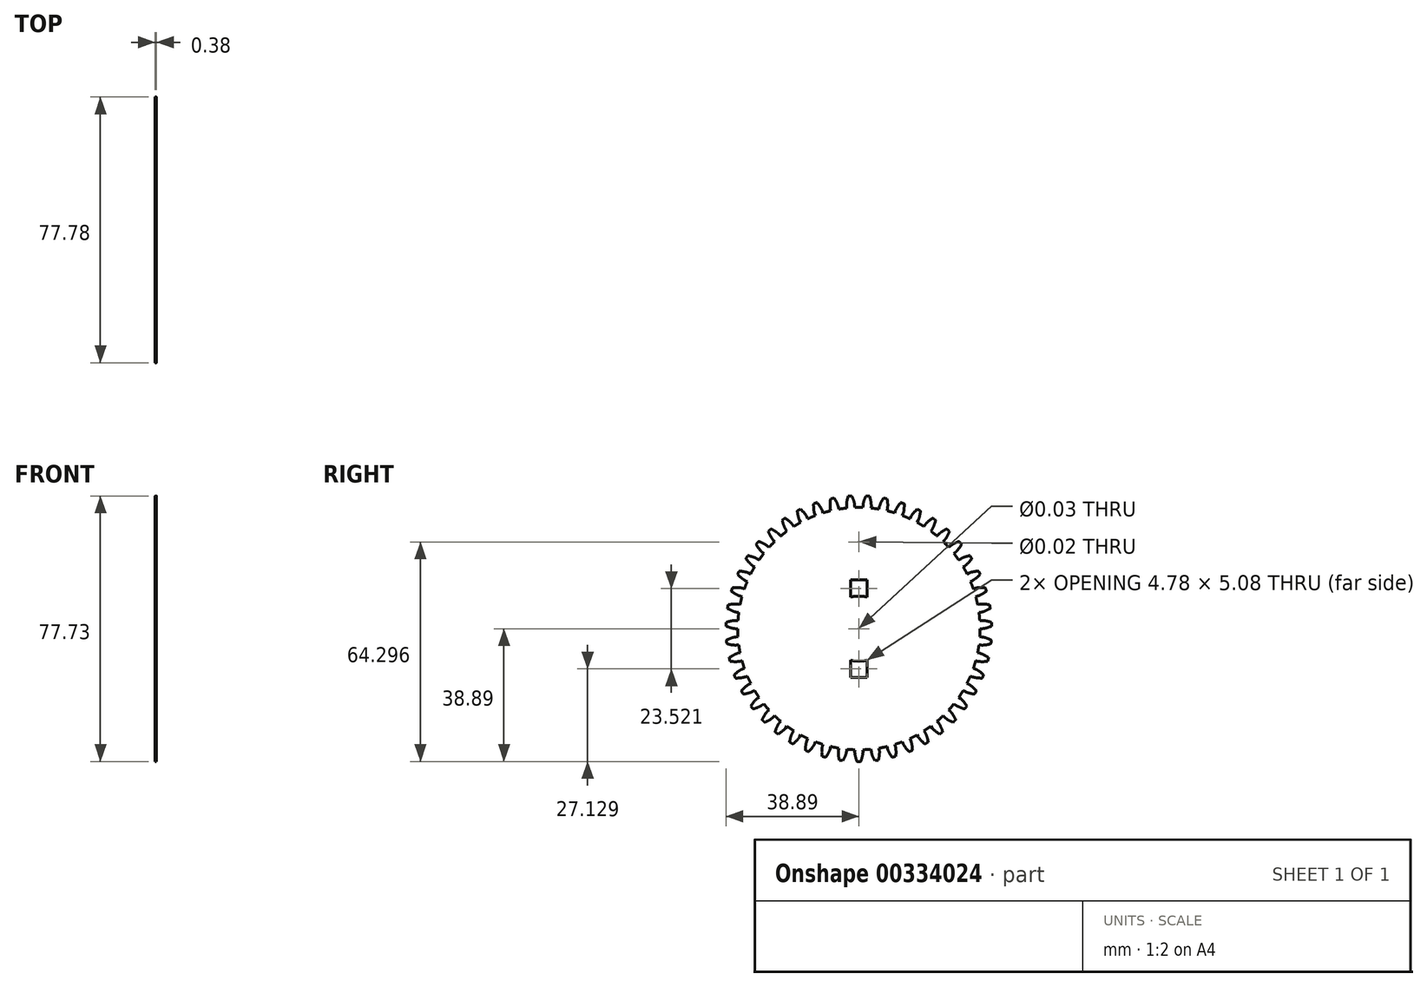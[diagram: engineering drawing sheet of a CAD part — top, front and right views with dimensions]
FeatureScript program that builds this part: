
annotation { "Feature Type Name" : "Feature", "Feature Type Description" : "" }
export const myFeature = defineFeature(function(context is Context, id is Id, definition is map)
    precondition{}
    {
        {
            assignVariable(context, id + "F0", {"name" : "NumberTeeth", "anyValue" : 47});
        }
        {
            assignVariable(context, id + "F1", {"name" : "GearThickness", "anyValue" : 0.38});
        }
        {
            var Q0;
            Q0=qCreatedBy(makeId("Right.planeOp"),FACE);
            var sketch = newSketch(context, id + "F2", { "sketchPlane" : qUnion([Q0])});
            skCircle(sketch, "E0", {"center": v(0, 0) * mm, "radius": 35.47 * mm});
            skCircle(sketch, "E1", {"center": v(0, 0) * mm, "radius": 36.12 * mm, "construction": true});
            skCircle(sketch, "E2", {"center": v(0, 0) * mm, "radius": 37.3 * mm, "construction": true});
            skCircle(sketch, "E3", {"center": v(0, 0) * mm, "radius": 38.9 * mm});
            skLineSegment(sketch, "E4", {"start": v(0, 0) * mm, "end": v(-36.12, 0) * mm, "construction": true});
            skLineSegment(sketch, "E5.1.0", {"start": v(0, 0) * mm, "end": v(-36.07, 1.8) * mm, "construction": true});
            skLineSegment(sketch, "E5.2.0", {"start": v(0, 0) * mm, "end": v(-35.94, 3.6) * mm, "construction": true});
            skLineSegment(sketch, "E5.3.0", {"start": v(0, 0) * mm, "end": v(-35.71, 5.4) * mm, "construction": true});
            skLineSegment(sketch, "E5.4.0", {"start": v(0, 0) * mm, "end": v(-35.4, 7.18) * mm, "construction": true});
            skLineSegment(sketch, "E5.5.0", {"start": v(0, 0) * mm, "end": v(-35, 8.94) * mm, "construction": true});
            skLineSegment(sketch, "E5.6.0", {"start": v(0, 0) * mm, "end": v(-34.5, 10.67) * mm, "construction": true});
            skLineSegment(sketch, "E5.7.0", {"start": v(0, 0) * mm, "end": v(-33.93, 12.38) * mm, "construction": true});
            skLineSegment(sketch, "E5.8.0", {"start": v(0, 0) * mm, "end": v(-33.27, 14.06) * mm, "construction": true});
            skLineSegment(sketch, "E5.9.0", {"start": v(0, 0) * mm, "end": v(-32.52, 15.71) * mm, "construction": true});
            skLineSegment(sketch, "E5.10.0", {"start": v(0, 0) * mm, "end": v(-31.7, 17.32) * mm, "construction": true});
            skLineSegment(sketch, "E5.11.0", {"start": v(0, 0) * mm, "end": v(-30.8, 18.88) * mm, "construction": true});
            skLineSegment(sketch, "E5.12.0", {"start": v(0, 0) * mm, "end": v(-29.8, 20.4) * mm, "construction": true});
            skLineSegment(sketch, "E5.13.0", {"start": v(0, 0) * mm, "end": v(-28.75, 21.86) * mm, "construction": true});
            skLineSegment(sketch, "E5.14.0", {"start": v(0, 0) * mm, "end": v(-27.62, 23.27) * mm, "construction": true});
            skLineSegment(sketch, "E5.anchor2", {"start": v(0, 0) * mm, "end": v(-27.62, 23.27) * mm, "construction": true});
            skLineSegment(sketch, "E6", {"start": v(-36.07, 1.8) * mm, "end": v(-36.16, 0) * mm, "construction": true});
            skLineSegment(sketch, "E7", {"start": v(-35.94, 3.6) * mm, "end": v(-36.3, 0.01) * mm, "construction": true});
            skLineSegment(sketch, "E8", {"start": v(-35.71, 5.4) * mm, "end": v(-36.52, 0.04) * mm, "construction": true});
            skLineSegment(sketch, "E9", {"start": v(-35, 8.94) * mm, "end": v(-37.23, 0.19) * mm, "construction": true});
            skLineSegment(sketch, "E10", {"start": v(-34.5, 10.67) * mm, "end": v(-37.7, 0.32) * mm, "construction": true});
            skLineSegment(sketch, "E11", {"start": v(-33.93, 12.38) * mm, "end": v(-38.26, 0.5) * mm, "construction": true});
            skLineSegment(sketch, "E12", {"start": v(-33.27, 14.06) * mm, "end": v(-38.9, 0.76) * mm, "construction": true});
            skLineSegment(sketch, "E13", {"start": v(-32.52, 15.71) * mm, "end": v(-39.6, 1.08) * mm, "construction": true});
            skLineSegment(sketch, "E14", {"start": v(-31.7, 17.32) * mm, "end": v(-40.35, 1.47) * mm, "construction": true});
            skLineSegment(sketch, "E15", {"start": v(-30.8, 18.88) * mm, "end": v(-41.17, 1.94) * mm, "construction": true});
            skLineSegment(sketch, "E16", {"start": v(-35.4, 7.18) * mm, "end": v(-36.83, 0.1) * mm, "construction": true});
            skLineSegment(sketch, "E17", {"start": v(-29.8, 20.4) * mm, "end": v(-42.05, 2.5) * mm, "construction": true});
            skLineSegment(sketch, "E18", {"start": v(-28.75, 21.86) * mm, "end": v(-42.96, 3.17) * mm, "construction": true});
            skLineSegment(sketch, "E19", {"start": v(-27.62, 23.27) * mm, "end": v(-43.91, 3.93) * mm, "construction": true});
            skLineSegment(sketch, "E20", {"start": v(0, 0) * mm, "end": v(-36.1, 1.2) * mm, "construction": true});
            skLineSegment(sketch, "E21", {"start": v(-35.47, 0) * mm, "end": v(-36.12, 0) * mm});
            skLineSegment(sketch, "E22.MirrorCS", {"start": v(-35.4, 2.37) * mm, "end": v(-36.04, 2.41) * mm});
            skFitSpline(sketch, "E23", {"points": [v(-36.12, 0) * mm, v(-36.16, 0) * mm, v(-36.3, 0.01) * mm, v(-36.52, 0.04) * mm, v(-36.83, 0.1) * mm, v(-37.23, 0.19) * mm, v(-37.7, 0.32) * mm, v(-38.26, 0.5) * mm, v(-38.9, 0.76) * mm, v(-39.6, 1.08) * mm, v(-40.35, 1.47) * mm, v(-41.17, 1.94) * mm, v(-42.05, 2.5) * mm, v(-42.96, 3.17) * mm, v(-43.91, 3.93) * mm], "startDerivative": vector(-0.68, 0) * mm, "endDerivative": vector(-1.75, 1.48) * mm});
            skLineSegment(sketch, "E24", {"start": v(-28.4, -9.14) * mm, "end": v(-43.91, 3.93) * mm, "construction": true});
            skFitSpline(sketch, "E25.MirrorCS", {"points": [v(-36.04, 2.41) * mm, v(-36.08, 2.41) * mm, v(-36.22, 2.41) * mm, v(-36.44, 2.4) * mm, v(-36.76, 2.36) * mm, v(-37.16, 2.3) * mm, v(-37.64, 2.2) * mm, v(-38.21, 2.05) * mm, v(-38.86, 1.84) * mm, v(-39.58, 1.57) * mm, v(-40.36, 1.23) * mm, v(-41.21, 0.81) * mm, v(-42.12, 0.3) * mm, v(-43.08, -0.3) * mm, v(-44.08, -0.99) * mm], "startDerivative": vector(-0.67, 0.05) * mm, "endDerivative": vector(-1.85, -1.36) * mm});
            skSolve(sketch);
        }
        {
            var Q0;
            {var subQ0=sQuery(id+"F2.wireOp",EDGE,"E0");var subQ27=makeQuery(id+"F2.imprint","INTERSECT",VERTEX,{"derivedFrom":[subQ0,sQuery(id+"F2.wireOp",EDGE,"10ea1024-8cf5-41f5-a75f-a634b86921f3.10.0")]});Q0=makeQuery(id+"F2.imprint","IMPRINT",FACE,{"disambiguationData":[TD([[makeQuery(id+"F2.imprint","IMPRINT",EDGE,{"disambiguationData":[TD([[subQ27,-1.0]])],"derivedFrom":subQ0}),1.0]])]});}
            var Q1;
            {var subQ0=sQuery(id+"F2.wireOp",EDGE,"10ea1024-8cf5-41f5-a75f-a634b86921f3.1.0");Q1=makeQuery(id+"F2.imprint","IMPRINT",FACE,{"disambiguationData":[TD([[makeQuery(id+"F2.imprint","IMPRINT",EDGE,{"derivedFrom":subQ0}),-1.0]])]});}
            var Q2;
            {var subQ7=sQuery(id+"F2.wireOp",EDGE,"10ea1024-8cf5-41f5-a75f-a634b86921f3.2.0");Q2=makeQuery(id+"F2.imprint","IMPRINT",FACE,{"disambiguationData":[TD([[makeQuery(id+"F2.imprint","IMPRINT",EDGE,{"derivedFrom":subQ7}),-1.0]])]});}
            var Q3;
            {var subQ8=sQuery(id+"F2.wireOp",EDGE,"10ea1024-8cf5-41f5-a75f-a634b86921f3.3.0");Q3=makeQuery(id+"F2.imprint","IMPRINT",FACE,{"disambiguationData":[TD([[makeQuery(id+"F2.imprint","IMPRINT",EDGE,{"derivedFrom":subQ8}),-1.0]])]});}
            var Q4;
            {var subQ2=sQuery(id+"F2.wireOp",EDGE,"10ea1024-8cf5-41f5-a75f-a634b86921f3.4.0");Q4=makeQuery(id+"F2.imprint","IMPRINT",FACE,{"disambiguationData":[TD([[makeQuery(id+"F2.imprint","IMPRINT",EDGE,{"derivedFrom":subQ2}),-1.0]])]});}
            var Q5;
            {var subQ8=sQuery(id+"F2.wireOp",EDGE,"10ea1024-8cf5-41f5-a75f-a634b86921f3.5.0");Q5=makeQuery(id+"F2.imprint","IMPRINT",FACE,{"disambiguationData":[TD([[makeQuery(id+"F2.imprint","IMPRINT",EDGE,{"derivedFrom":subQ8}),-1.0]])]});}
            var Q6;
            {var subQ3=sQuery(id+"F2.wireOp",EDGE,"10ea1024-8cf5-41f5-a75f-a634b86921f3.6.0");Q6=makeQuery(id+"F2.imprint","IMPRINT",FACE,{"disambiguationData":[TD([[makeQuery(id+"F2.imprint","IMPRINT",EDGE,{"derivedFrom":subQ3}),-1.0]])]});}
            var Q7;
            {var subQ0=sQuery(id+"F2.wireOp",EDGE,"10ea1024-8cf5-41f5-a75f-a634b86921f3.7.0");Q7=makeQuery(id+"F2.imprint","IMPRINT",FACE,{"disambiguationData":[TD([[makeQuery(id+"F2.imprint","IMPRINT",EDGE,{"derivedFrom":subQ0}),-1.0]])]});}
            var Q8;
            {var subQ5=sQuery(id+"F2.wireOp",EDGE,"10ea1024-8cf5-41f5-a75f-a634b86921f3.8.0");Q8=makeQuery(id+"F2.imprint","IMPRINT",FACE,{"disambiguationData":[TD([[makeQuery(id+"F2.imprint","IMPRINT",EDGE,{"derivedFrom":subQ5}),-1.0]])]});}
            var Q9;
            {var subQ1=sQuery(id+"F2.wireOp",EDGE,"10ea1024-8cf5-41f5-a75f-a634b86921f3.9.0");Q9=makeQuery(id+"F2.imprint","IMPRINT",FACE,{"disambiguationData":[TD([[makeQuery(id+"F2.imprint","IMPRINT",EDGE,{"derivedFrom":subQ1}),-1.0]])]});}
            var Q10;
            {var subQ5=sQuery(id+"F2.wireOp",EDGE,"10ea1024-8cf5-41f5-a75f-a634b86921f3.10.0");Q10=makeQuery(id+"F2.imprint","IMPRINT",FACE,{"disambiguationData":[TD([[makeQuery(id+"F2.imprint","IMPRINT",EDGE,{"derivedFrom":subQ5}),-1.0]])]});}
            var Q11;
            {var subQ8=sQuery(id+"F2.wireOp",EDGE,"10ea1024-8cf5-41f5-a75f-a634b86921f3.11.0");Q11=makeQuery(id+"F2.imprint","IMPRINT",FACE,{"disambiguationData":[TD([[makeQuery(id+"F2.imprint","IMPRINT",EDGE,{"derivedFrom":subQ8}),-1.0]])]});}
            var Q12;
            {var subQ2=sQuery(id+"F2.wireOp",EDGE,"10ea1024-8cf5-41f5-a75f-a634b86921f3.12.0");Q12=makeQuery(id+"F2.imprint","IMPRINT",FACE,{"disambiguationData":[TD([[makeQuery(id+"F2.imprint","IMPRINT",EDGE,{"derivedFrom":subQ2}),-1.0]])]});}
            var Q13;
            {var subQ3=sQuery(id+"F2.wireOp",EDGE,"10ea1024-8cf5-41f5-a75f-a634b86921f3.13.0");Q13=makeQuery(id+"F2.imprint","IMPRINT",FACE,{"disambiguationData":[TD([[makeQuery(id+"F2.imprint","IMPRINT",EDGE,{"derivedFrom":subQ3}),-1.0]])]});}
            var Q14;
            {var subQ0=sQuery(id+"F2.wireOp",EDGE,"10ea1024-8cf5-41f5-a75f-a634b86921f3.14.0");Q14=makeQuery(id+"F2.imprint","IMPRINT",FACE,{"disambiguationData":[TD([[makeQuery(id+"F2.imprint","IMPRINT",EDGE,{"derivedFrom":subQ0}),-1.0]])]});}
            var Q15;
            {var subQ6=sQuery(id+"F2.wireOp",EDGE,"10ea1024-8cf5-41f5-a75f-a634b86921f3.15.0");Q15=makeQuery(id+"F2.imprint","IMPRINT",FACE,{"disambiguationData":[TD([[makeQuery(id+"F2.imprint","IMPRINT",EDGE,{"derivedFrom":subQ6}),-1.0]])]});}
            var Q16;
            {var subQ5=sQuery(id+"F2.wireOp",EDGE,"10ea1024-8cf5-41f5-a75f-a634b86921f3.16.0");Q16=makeQuery(id+"F2.imprint","IMPRINT",FACE,{"disambiguationData":[TD([[makeQuery(id+"F2.imprint","IMPRINT",EDGE,{"derivedFrom":subQ5}),-1.0]])]});}
            var Q17;
            {var subQ7=sQuery(id+"F2.wireOp",EDGE,"10ea1024-8cf5-41f5-a75f-a634b86921f3.17.0");Q17=makeQuery(id+"F2.imprint","IMPRINT",FACE,{"disambiguationData":[TD([[makeQuery(id+"F2.imprint","IMPRINT",EDGE,{"derivedFrom":subQ7}),-1.0]])]});}
            var Q18;
            {var subQ5=sQuery(id+"F2.wireOp",EDGE,"10ea1024-8cf5-41f5-a75f-a634b86921f3.18.0");Q18=makeQuery(id+"F2.imprint","IMPRINT",FACE,{"disambiguationData":[TD([[makeQuery(id+"F2.imprint","IMPRINT",EDGE,{"derivedFrom":subQ5}),-1.0]])]});}
            var Q19;
            {var subQ8=sQuery(id+"F2.wireOp",EDGE,"10ea1024-8cf5-41f5-a75f-a634b86921f3.19.0");Q19=makeQuery(id+"F2.imprint","IMPRINT",FACE,{"disambiguationData":[TD([[makeQuery(id+"F2.imprint","IMPRINT",EDGE,{"derivedFrom":subQ8}),-1.0]])]});}
            var Q20;
            {var subQ8=sQuery(id+"F2.wireOp",EDGE,"E21");Q20=makeQuery(id+"F2.imprint","IMPRINT",FACE,{"disambiguationData":[TD([[makeQuery(id+"F2.imprint","IMPRINT",EDGE,{"derivedFrom":subQ8}),-1.0]])]});}
            extrude(context, id + "F3", {"entities" : qUnion([Q0, Q1, Q2, Q3, Q4, Q5, Q6, Q7, Q8, Q9, Q10, Q11, Q12, Q13, Q14, Q15, Q16, Q17, Q18, Q19, Q20]), "depth" : (getVariable(context, 'GearThickness')) * mm});
        }
        {
            var Q0;
            Q0=makeQuery(id+"F3.opExtrude","SWEPT_FACE",FACE,{"disambiguationData":[OSD([sQuery(id+"F2.wireOp",EDGE,"E25.MirrorCS")])]});
            var Q1;
            Q1=makeQuery(id+"F3.opExtrude","SWEPT_FACE",FACE,{"disambiguationData":[OSD([sQuery(id+"F2.wireOp",EDGE,"E23")])]});
            var Q2;
            Q2=makeQuery(id+"F3.opExtrude","SWEPT_FACE",FACE,{"disambiguationData":[OSD([sQuery(id+"F2.wireOp",EDGE,"E3")])]});
            var Q3;
            Q3=makeQuery(id+"F3.opExtrude","SWEPT_FACE",FACE,{"disambiguationData":[OSD([sQuery(id+"F2.wireOp",EDGE,"E22.MirrorCS")])]});
            var Q4;
            Q4=makeQuery(id+"F3.opExtrude","SWEPT_FACE",FACE,{"disambiguationData":[OSD([sQuery(id+"F2.wireOp",EDGE,"E21")])]});
            var Q5;
            Q5=makeQuery(id+"F3.opExtrude","SWEPT_FACE",FACE,{"disambiguationData":[OSD([sQuery(id+"F2.wireOp",EDGE,"E0")])]});
            circularPattern(context, id + "F4", {"faces" : qUnion([Q0, Q1, Q2, Q3, Q4]), "axis" : qUnion([Q5]), "angle" : 360 * degree, "instanceCount" : getVariable(context, 'NumberTeeth'), "equalSpace" : true, "patternType" : PatternType.FACE});
        }
        {
            var Q0;
            Q0=sQuery(id+"F2.wireOp",VERTEX,"E0.center");
            var Q1;
            Q1=makeQuery(id+"F3.opExtrude","SWEPT_BODY",BODY,{"disambiguationData":[OSD([sQuery(id+"F2.wireOp",EDGE,"E0"),sQuery(id+"F2.wireOp",EDGE,"E3"),sQuery(id+"F2.wireOp",EDGE,"E21"),sQuery(id+"F2.wireOp",EDGE,"E22.MirrorCS"),sQuery(id+"F2.wireOp",EDGE,"E23"),sQuery(id+"F2.wireOp",EDGE,"E25.MirrorCS")])]});
            hole(context, id + "F5", {"style" : HoleStyle.SIMPLE, "endStyle" : HoleEndStyle.THROUGH, "oppositeDirection" : true, "standardTappedOrClearance" : lookupTablePath({ "standard" : "ANSI", "size" : "3/4 (0.75)", "type" : "Drilled" }), "standardBlindInLast" : lookupTablePath({ "standard" : "ANSI", "size" : "3/4", "type" : "Drilled" }), "holeDiameter" : 3 / 101.6 * mm, "tappedDepth" : 12.7 * mm, "tapClearance" : 3, "locations" : qUnion([Q0]), "scope" : qUnion([Q1])});
        }
        {
            var Q0;
            Q0=makeQuery(id+"F3.opExtrude","CAP_FACE",FACE,{"disambiguationData":[OSD([sQuery(id+"F2.wireOp",EDGE,"E0"),sQuery(id+"F2.wireOp",EDGE,"E3"),sQuery(id+"F2.wireOp",EDGE,"E21"),sQuery(id+"F2.wireOp",EDGE,"E22.MirrorCS"),sQuery(id+"F2.wireOp",EDGE,"E23"),sQuery(id+"F2.wireOp",EDGE,"E25.MirrorCS")])],"isStart":true});
            var sketch = newSketch(context, id + "F6", { "sketchPlane" : qUnion([Q0])});
            skCircle(sketch, "E26.0", {"center": v(0, 0) * mm, "radius": 9.52 * mm});
            skLineSegment(sketch, "E27.bottom", {"start": v(2.39, -14.3) * mm, "end": v(-2.39, -14.3) * mm});
            skLineSegment(sketch, "E27.top", {"start": v(2.39, 14.3) * mm, "end": v(-2.39, 14.3) * mm});
            skLineSegment(sketch, "E27.left", {"start": v(2.39, -14.3) * mm, "end": v(2.39, 14.3) * mm});
            skLineSegment(sketch, "E27.right", {"start": v(-2.39, -14.3) * mm, "end": v(-2.39, 14.3) * mm});
            skPoint(sketch, "E28", {"position": v(0, 25.4) * mm});
            skSolve(sketch);
        }
        {
            var Q0;
            {var subQ5=sQuery(id+"F6.wireOp",EDGE,"E27.bottom");Q0=makeQuery(id+"F6.imprint","IMPRINT",FACE,{"disambiguationData":[TD([[makeQuery(id+"F6.imprint","IMPRINT",EDGE,{"derivedFrom":subQ5}),-1.0]])]});}
            var Q1;
            {var subQ5=sQuery(id+"F6.wireOp",EDGE,"E27.top");Q1=makeQuery(id+"F6.imprint","IMPRINT",FACE,{"disambiguationData":[TD([[makeQuery(id+"F6.imprint","IMPRINT",EDGE,{"derivedFrom":subQ5}),1.0]])]});}
            extrude(context, id + "F7", {"entities" : qUnion([Q0, Q1]), "operationType" : NewBodyOperationType.REMOVE, "endBound" : BoundingType.UP_TO_NEXT, "oppositeDirection" : true, "depth" : 25.4 * mm});
        }
        {
            var Q0;
            Q0=sQuery(id+"F6.wireOp",VERTEX,"E28");
            var Q1;
            Q1=makeQuery(id+"F3.opExtrude","SWEPT_BODY",BODY,{"disambiguationData":[OSD([sQuery(id+"F2.wireOp",EDGE,"E0"),sQuery(id+"F2.wireOp",EDGE,"E3"),sQuery(id+"F2.wireOp",EDGE,"E21"),sQuery(id+"F2.wireOp",EDGE,"E22.MirrorCS"),sQuery(id+"F2.wireOp",EDGE,"E23"),sQuery(id+"F2.wireOp",EDGE,"E25.MirrorCS")])]});
            hole(context, id + "F8", {"style" : HoleStyle.SIMPLE, "endStyle" : HoleEndStyle.THROUGH, "standardTappedOrClearance" : lookupTablePath({ "standard" : "ANSI", "size" : "1/2 (0.5)", "type" : "Drilled" }), "standardBlindInLast" : lookupTablePath({ "standard" : "ANSI", "size" : "1/2", "type" : "Drilled" }), "holeDiameter" : 1 / 50.8 * mm, "tappedDepth" : 12.7 * mm, "tapClearance" : 3, "locations" : qUnion([Q0]), "scope" : qUnion([Q1])});
        }
    });
